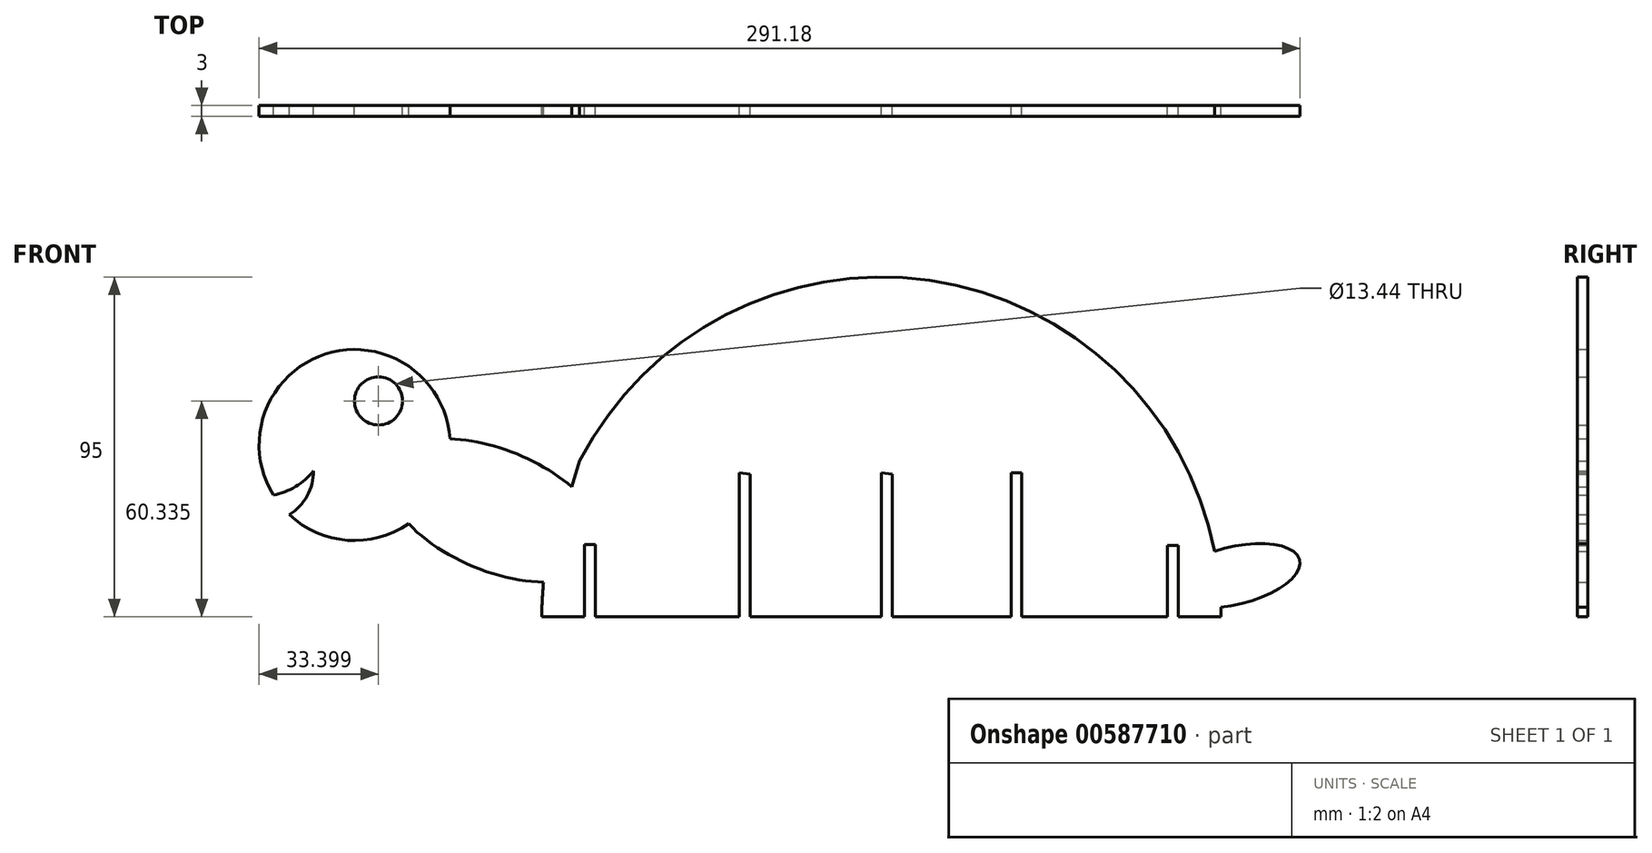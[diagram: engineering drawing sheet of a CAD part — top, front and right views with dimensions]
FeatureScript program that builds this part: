
annotation { "Feature Type Name" : "Feature", "Feature Type Description" : "" }
export const myFeature = defineFeature(function(context is Context, id is Id, definition is map)
    precondition{}
    {
        {
            var Q0;
            Q0=qCreatedBy(makeId("Front.planeOp"),FACE);
            var sketch = newSketch(context, id + "F0", { "sketchPlane" : qUnion([Q0])});
            skLineSegment(sketch, "E0", {"start": v(100.32, 0) * mm, "end": v(88.32, 0) * mm});
            skArc(sketch, "E1", {"start": v(100.32, 0) * mm, "mid": v(100.3, 1.36) * mm, "end": v(100.28, 2.72) * mm});
            skArc(sketch, "E2.trimOffspring", {"start": v(-89.03, 11.13) * mm, "mid": v(-89.52, 5.57) * mm, "end": v(-89.68, 0) * mm});
            skEllipticalArc(sketch, "E3", {});
            skArc(sketch, "E4.trimOffspring", {"start": v(98.55, 18.26) * mm, "mid": v(18.73, 94.05) * mm, "end": v(-79.1, 43.6) * mm});
            skPoint(sketch, "E5", {"position": v(-100.44, 47.2) * mm});
            skLineSegment(sketch, "E6", {"start": v(-79.1, 43.6) * mm, "end": v(-81.32, 36.3) * mm});
            skEllipticalArc(sketch, "E7", {});
            skArc(sketch, "E8", {"start": v(-115.4, 49.77) * mm, "mid": v(-150.18, 73.47) * mm, "end": v(-164.8, 34) * mm});
            skEllipticalArc(sketch, "E9.trimOffspring", {});
            skCircle(sketch, "E10", {"center": v(-135.37, 60.34) * mm, "radius": 6.72 * mm});
            skLineSegment(sketch, "E11", {"start": v(-89.68, 0) * mm, "end": v(-77.68, 0) * mm});
            skLineSegment(sketch, "E12", {"start": v(-74.68, 0) * mm, "end": v(-34.4, 0) * mm});
            skLineSegment(sketch, "E13", {"start": v(85.32, 0) * mm, "end": v(44.6, 0) * mm});
            skLineSegment(sketch, "E14", {"start": v(41.6, 0) * mm, "end": v(8.32, 0) * mm});
            skLineSegment(sketch, "E15", {"start": v(5.32, 0) * mm, "end": v(-31.4, 0) * mm});
            skLineSegment(sketch, "E16", {"start": v(-74.68, 0) * mm, "end": v(-74.68, 20.23) * mm});
            skLineSegment(sketch, "E17", {"start": v(85.32, 0) * mm, "end": v(85.32, 19.87) * mm});
            skPoint(sketch, "E18", {"position": v(-77.68, 0) * mm});
            skLineSegment(sketch, "E19", {"start": v(-77.68, 0) * mm, "end": v(-77.68, 20.23) * mm});
            skLineSegment(sketch, "E20", {"start": v(-77.68, 20.23) * mm, "end": v(-74.68, 20.23) * mm});
            skPoint(sketch, "E21", {"position": v(88.32, 0) * mm});
            skLineSegment(sketch, "E22", {"start": v(88.32, 0) * mm, "end": v(88.32, 19.87) * mm});
            skLineSegment(sketch, "E23", {"start": v(88.32, 19.87) * mm, "end": v(85.32, 19.87) * mm});
            skLineSegment(sketch, "E24", {"start": v(-34.4, 0) * mm, "end": v(-34.4, 40.28) * mm});
            skLineSegment(sketch, "E25", {"start": v(5.32, 0) * mm, "end": v(5.32, 40.28) * mm});
            skLineSegment(sketch, "E26", {"start": v(44.6, 0) * mm, "end": v(44.6, 40.28) * mm});
            skPoint(sketch, "E27", {"position": v(41.6, 0) * mm});
            skLineSegment(sketch, "E28", {"start": v(41.6, 0) * mm, "end": v(41.6, 40.28) * mm});
            skLineSegment(sketch, "E29", {"start": v(41.6, 40.28) * mm, "end": v(44.6, 40.28) * mm});
            skPoint(sketch, "E30", {"position": v(8.32, 0) * mm});
            skLineSegment(sketch, "E31", {"start": v(8.32, 0) * mm, "end": v(8.32, 39.93) * mm});
            skLineSegment(sketch, "E32", {"start": v(8.32, 39.93) * mm, "end": v(5.32, 40.28) * mm});
            skPoint(sketch, "E33", {"position": v(-31.4, 0) * mm});
            skLineSegment(sketch, "E34", {"start": v(-31.4, 0) * mm, "end": v(-31.4, 39.93) * mm});
            skLineSegment(sketch, "E35", {"start": v(-31.4, 39.93) * mm, "end": v(-34.4, 40.28) * mm});
            skLineSegment(sketch, "E36.trimOffspring", {"start": v(-34.4, 0) * mm, "end": v(-74.68, 0) * mm});
            skLineSegment(sketch, "E37.trimOffspring", {"start": v(-77.68, 0) * mm, "end": v(-89.68, 0) * mm});
            skArc(sketch, "E38", {"start": v(-164.8, 34) * mm, "mid": v(-158.26, 36.6) * mm, "end": v(-153.12, 41.39) * mm});
            skArc(sketch, "E39.trimOffspring", {"start": v(-160.33, 28.54) * mm, "mid": v(-144.1, 21.38) * mm, "end": v(-126.95, 25.99) * mm});
            skArc(sketch, "E40", {"start": v(-160.33, 28.54) * mm, "mid": v(-155.33, 33.78) * mm, "end": v(-153.56, 40.8) * mm});
            const initialGuessF0  = {"E3": [0.10418568551540375, 0.011512231081724167, 0.9728062168298889, 0.23162051829904706, 0.018638617259337326, 0.008055484397385654, 4.393831366726673, 1.7828546852865044], "E7": [-0.10265056788921356, 0.029725544154644012, 0.9208176430315056, -0.38999342081874006, 0.032477638261886654, 0.016887533074783013, 4.0125769571110785, 5.3843103583524945], "E9.trimOffspring": [-0.10265056788921356, 0.029725544154644012, 0.9208176430315056, -0.38999342081874006, 0.032477638261886654, 0.016887533074783013, 1.017170301926875, 2.216950804548891]};
            skSetInitialGuess(sketch, initialGuessF0);
            skSolve(sketch);
        }
        {
            var Q0;
            Q0=qSketchRegion(id+"F0",true);
            extrude(context, id + "F1", {"entities" : qUnion([Q0]), "depth" : 3 * mm, "offsetDistance" : 25 * mm});
        }
    });
